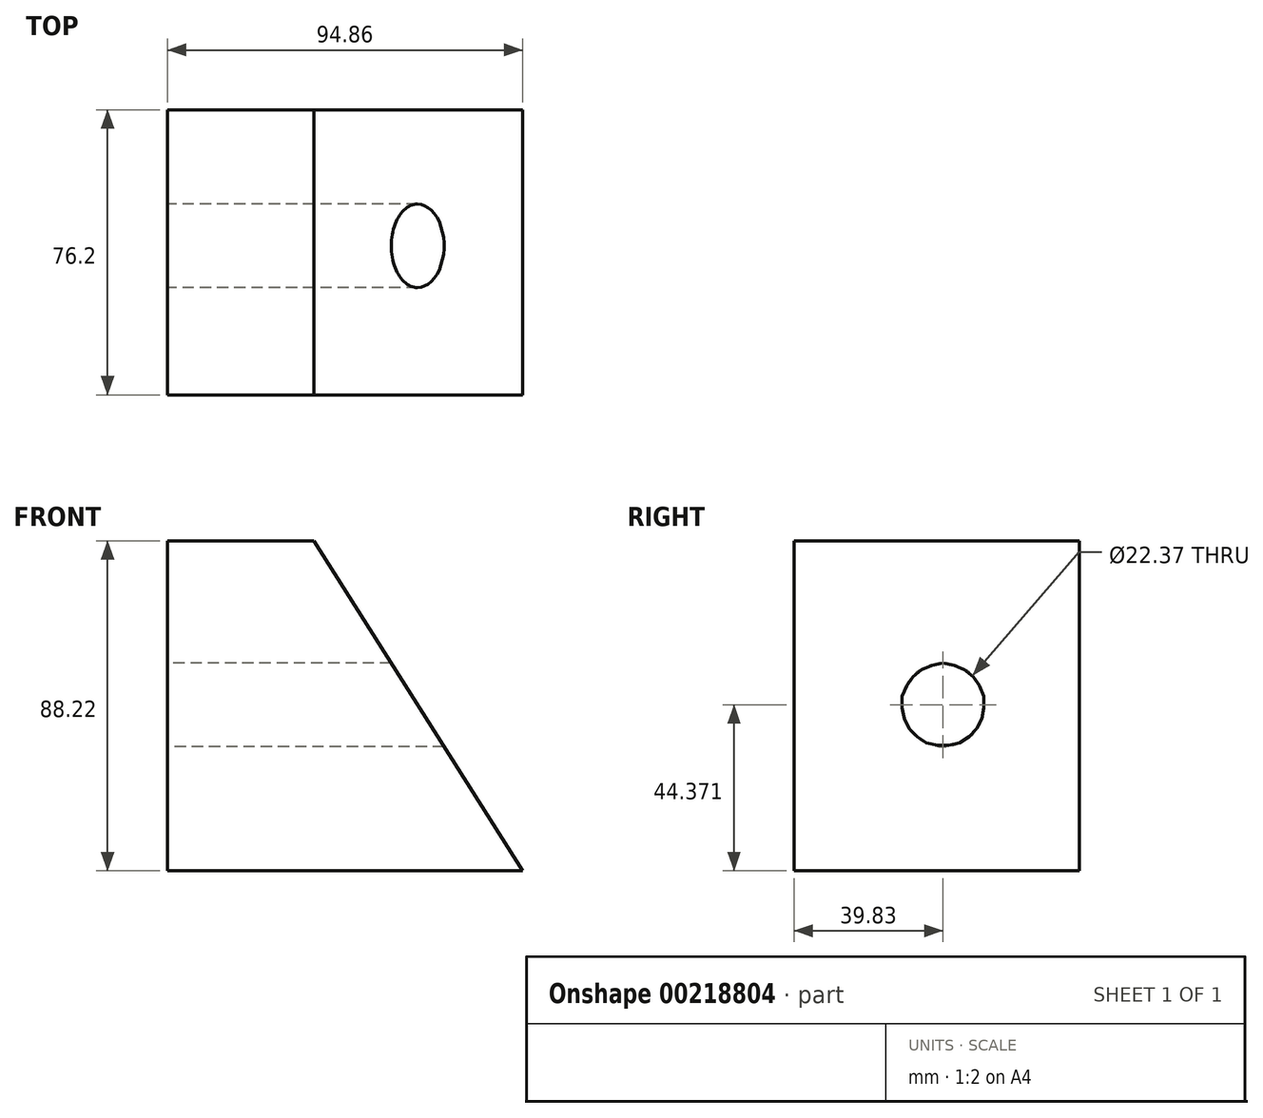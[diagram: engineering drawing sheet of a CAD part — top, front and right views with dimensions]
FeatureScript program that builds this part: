
annotation { "Feature Type Name" : "Feature", "Feature Type Description" : "" }
export const myFeature = defineFeature(function(context is Context, id is Id, definition is map)
    precondition{}
    {
        {
            var Q0;
            Q0=qCreatedBy(makeId("Front.planeOp"),FACE);
            var sketch = newSketch(context, id + "F0", { "sketchPlane" : qUnion([Q0])});
            skLineSegment(sketch, "E0", {"start": v(-34.94, 50.4) * mm, "end": v(-34.94, -37.82) * mm});
            skLineSegment(sketch, "E1", {"start": v(-34.94, -37.82) * mm, "end": v(59.92, -37.82) * mm});
            skLineSegment(sketch, "E2", {"start": v(59.92, -37.82) * mm, "end": v(4.2, 50.4) * mm});
            skLineSegment(sketch, "E3", {"start": v(4.2, 50.4) * mm, "end": v(-34.94, 50.4) * mm});
            skSolve(sketch);
        }
        {
            var Q0;
            Q0 = qSketchRegion(id + "F0", true);
            extrude(context, id + "F1", {"entities" : qUnion([Q0]), "oppositeDirection" : true, "depth" : 76.2 * mm});
        }
        {
            var Q0;
            Q0=qCreatedBy(makeId("Right.planeOp"),FACE);
            var sketch = newSketch(context, id + "F2", { "sketchPlane" : qUnion([Q0])});
            skCircle(sketch, "E4", {"center": v(39.83, 6.55) * mm, "radius": 11.19 * mm});
            skSolve(sketch);
        }
        {
            var Q0;
            Q0 = qSketchRegion(id + "F2", true);
            extrude(context, id + "F3", {"entities" : qUnion([Q0]), "operationType" : NewBodyOperationType.REMOVE, "endBound" : BoundingType.SYMMETRIC, "depth" : 228.6 * mm});
        }
    });
